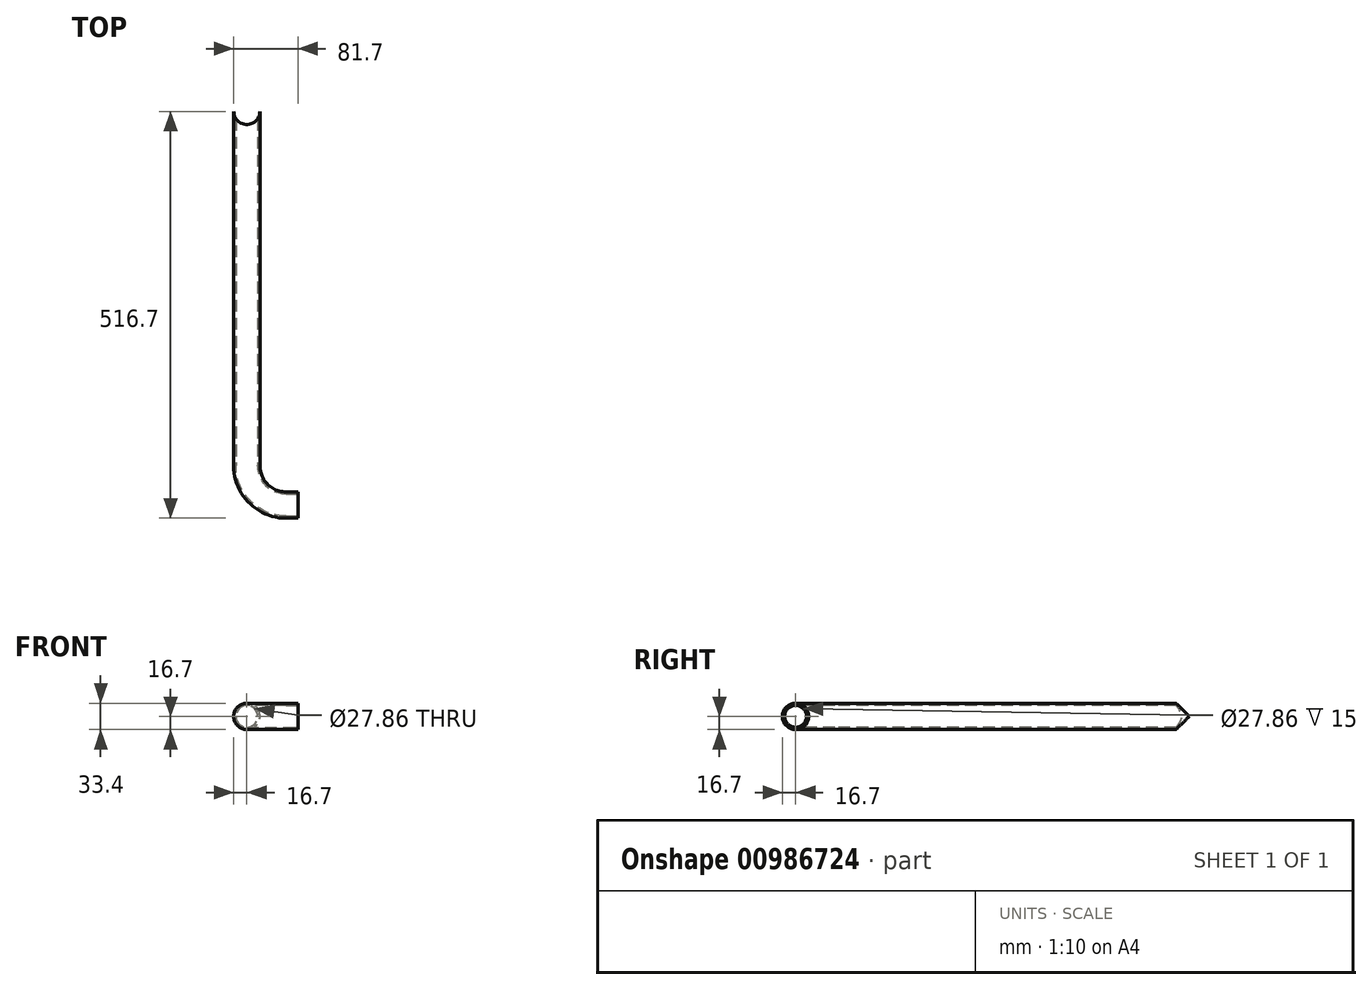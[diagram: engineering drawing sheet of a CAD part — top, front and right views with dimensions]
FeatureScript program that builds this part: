
annotation { "Feature Type Name" : "Feature", "Feature Type Description" : "" }
export const myFeature = defineFeature(function(context is Context, id is Id, definition is map)
    precondition{}
    {
        {
            var Q0;
            Q0=qCreatedBy(makeId("Top.planeOp"),FACE);
            var sketch = newSketch(context, id + "F0", { "sketchPlane" : qUnion([Q0])});
            skLineSegment(sketch, "E0", {"start": v(0, 0) * mm, "end": v(0, -450) * mm});
            skPoint(sketch, "E1.visualSharp", {"position": v(0, -500) * mm});
            skLineSegment(sketch, "E2", {"start": v(50, -500) * mm, "end": v(65, -500) * mm});
            skArc(sketch, "E3.filletArc", {"start": v(0, -450) * mm, "mid": v(14.64, -485.36) * mm, "end": v(50, -500) * mm});
            skSolve(sketch);
        }
        {
            var Q0;
            Q0=qCreatedBy(makeId("Front.planeOp"),FACE);
            var sketch = newSketch(context, id + "F1", { "sketchPlane" : qUnion([Q0])});
            skCircle(sketch, "E4", {"center": v(0, 0) * mm, "radius": 16.7 * mm});
            skCircle(sketch, "E5.0", {"center": v(0, 0) * mm, "radius": 13.93 * mm});
            skSolve(sketch);
        }
        {
            var Q0;
            Q0=makeQuery(id+"F1.imprint","IMPRINT",FACE,{"disambiguationData":[TD([[makeQuery(id+"F1.imprint","IMPRINT",EDGE,{"derivedFrom":sQuery(id+"F1.wireOp",EDGE,"E4")}),1.0]])]});
            var Q1;
            Q1=sQuery(id+"F0.wireOp",EDGE,"E0");
            var Q2;
            Q2=sQuery(id+"F0.wireOp",EDGE,"E3.filletArc");
            var Q3;
            Q3=sQuery(id+"F0.wireOp",EDGE,"E2");
            sweep(context, id + "F2", {"profiles" : qUnion([Q0]), "path" : qUnion([Q1, Q2, Q3])});
        }
        {
            var Q0;
            Q0=qCreatedBy(makeId("Top.planeOp"),FACE);
            var sketch = newSketch(context, id + "F3", { "sketchPlane" : qUnion([Q0])});
            skCircle(sketch, "E6", {"center": v(0, 0) * mm, "radius": 16.7 * mm});
            skSolve(sketch);
        }
        {
            var Q0;
            Q0=qSketchRegion(id+"F3",true);
            extrude(context, id + "F4", {"entities" : qUnion([Q0]), "operationType" : NewBodyOperationType.REMOVE, "oppositeDirection" : true, "depth" : 25 * mm, "offsetDistance" : 25 * mm, "hasSecondDirection" : true, "secondDirectionOppositeDirection" : false, "secondDirectionDepth" : 25 * mm});
        }
    });
